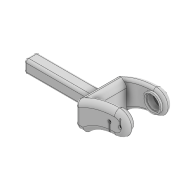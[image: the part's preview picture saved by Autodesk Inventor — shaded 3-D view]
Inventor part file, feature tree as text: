
AUTODESK INVENTOR PART (.ipt)
format: ipt  version: 2020 (Build 240168000, 168)  size: 456,704 bytes
history: native  units: mm
features: fillet x9, extrude x8, sketch x8, mirror x2, projected_geometry x1, plane x1
ambient origin geometry x8: Origin, YZ Plane, XZ Plane, XY Plane, X Axis, Y Axis, Z Axis, Center Point
bodies: Solid1 (feature_tree)
feature tree (29):
  extrude  "Extrusion1"  Depth=13.5mm
  extrude  "Extrusion2"  Depth=9.0mm
  extrude  "Extrusion3"  Depth=10.0mm
  fillet  "Fillet3"  Radius=9.0mm
  fillet  "Fillet4"  Radius=10.0mm
  extrude  "Extrusion4"  Depth=2.0mm
  extrude  "Extrusion5"  Depth=5.0mm
  extrude  "Extrusion6"  Depth=2.0mm TaperAngle=0.0deg
  fillet  "Fillet5"  Radius=6.0mm
  fillet  "Fillet6"  Radius=15.0mm
  extrude  "Extrusion7"  Depth=2.5mm
  fillet  "Fillet7"  Radius=26.0mm
  mirror  "Mirror1"
  extrude  "Extrusion8"  Depth=2.0mm
  mirror  "Mirror2"
  fillet  "Fillet8"  Radius=2.0mm
  fillet  "Fillet9"  Radius=5.2mm
  fillet  "Fillet10"  Radius=2.4mm
  fillet  "Fillet11"  Radius=5.2mm
  sketch  "Sketch1"  dims[d0=46.0mm d1=13.5mm]
  sketch  "Sketch2"  dims[d2=18.0mm d3=0.0mm d4=9.0mm]
  sketch  "Sketch3"  dims[d5=4.5mm d6=5.0mm d7=9.0mm d8=10.0mm]
  sketch  "Sketch4"  dims[d9=5.0mm d10=2.0mm]
  sketch  "Sketch5"  dims[d11=4.0mm d12=5.0mm]
  sketch  "Sketch6"  dims[d13=2.0mm d14=18.0mm d15=0.0mm d17=6.0mm d18=15.0mm]
  projected_geometry  "Projected Loop1"
  sketch  "Sketch7"  dims[d19=12.0mm d20=2.5mm d21=26.0mm]
  plane  "Work Plane1"
  sketch  "Sketch8"  dims[d22=18.0mm d23=0.0mm d25=2.0mm d26=2.0mm d27=5.2mm d28=2.4mm d29=0.0mm d30=5.2mm d31=2.4mm d32=0.0mm d33=2.0mm d34=20.4mm d35=1.2mm d36=0.0mm d37=0.0mm d38=1.0mm d39=1.0mm d40=7.0mm d41=6.0mm d42=1.0mm d43=0.0mm d44=0.5mm d45=0.0mm d46=0.25mm d47=0.2mm d48=0.24mm d49=0.0mm d50=0.25mm d51=5.0mm d52=4.0mm d53=2.0mm d54=1.75mm d55=1.0mm d56=1.0mm]
